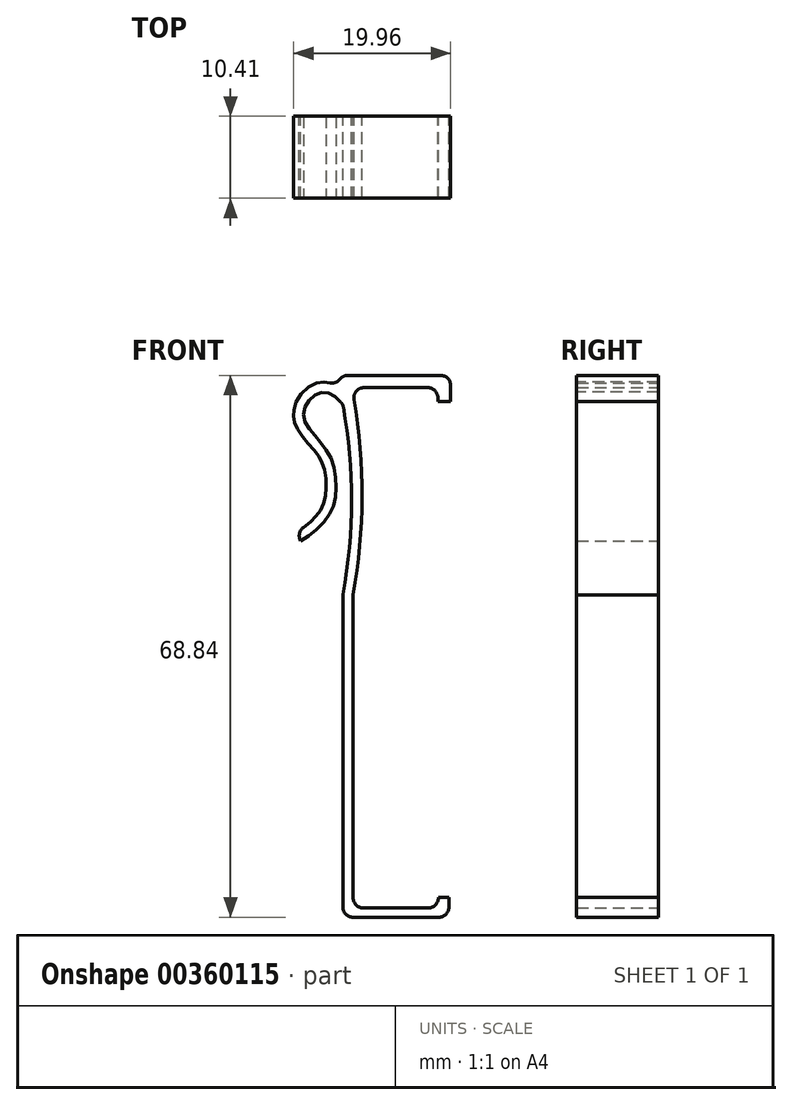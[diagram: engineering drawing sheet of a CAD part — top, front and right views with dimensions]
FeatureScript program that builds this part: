
annotation { "Feature Type Name" : "Feature", "Feature Type Description" : "" }
export const myFeature = defineFeature(function(context is Context, id is Id, definition is map)
    precondition{}
    {
        {
            var Q0;
            Q0=qCreatedBy(makeId("Front.planeOp"),FACE);
            var sketch = newSketch(context, id + "F0", { "sketchPlane" : qUnion([Q0])});
            skLineSegment(sketch, "E0", {"start": v(5, -38.43) * mm, "end": v(5, -40.97) * mm});
            skLineSegment(sketch, "E1", {"start": v(5, -40.97) * mm, "end": v(-8.46, -40.97) * mm});
            skLineSegment(sketch, "E2", {"start": v(-8.46, -40.97) * mm, "end": v(-8.46, 0.05) * mm});
            skFitSpline(sketch, "E3", {"points": [v(-8.49, 24.22) * mm, v(-10.38, 25.67) * mm, v(-12.43, 25.03) * mm, v(-13.45, 22.73) * mm, v(-12.1, 20.3) * mm, v(-10, 17.35) * mm, v(-9.36, 13.05) * mm, v(-10.53, 9.66) * mm, v(-13.86, 6.85) * mm], "startDerivative": vector(-14.07, 14.82) * mm, "endDerivative": vector(-23.04, -10.91) * mm});
            skFitSpline(sketch, "E4.0", {"points": [v(-7.57, 25.1) * mm, v(-7.7, 25.24) * mm, v(-8.04, 25.6) * mm, v(-8.57, 26.1) * mm, v(-9.1, 26.48) * mm, v(-9.47, 26.69) * mm, v(-9.8, 26.83) * mm, v(-10.08, 26.91) * mm, v(-10.36, 26.97) * mm, v(-10.74, 27.01) * mm, v(-11.2, 27) * mm, v(-11.9, 26.85) * mm, v(-12.69, 26.48) * mm, v(-13.49, 25.83) * mm, v(-14.12, 25.02) * mm, v(-14.5, 24.24) * mm, v(-14.68, 23.56) * mm, v(-14.73, 23.1) * mm, v(-14.73, 22.73) * mm, v(-14.7, 22.36) * mm, v(-14.6, 21.92) * mm, v(-14.42, 21.43) * mm, v(-14.12, 20.84) * mm, v(-13.68, 20.2) * mm, v(-13.11, 19.51) * mm, v(-12.57, 18.89) * mm, v(-12.06, 18.29) * mm, v(-11.61, 17.7) * mm, v(-11.31, 17.18) * mm, v(-11.12, 16.76) * mm, v(-10.95, 16.3) * mm, v(-10.77, 15.66) * mm, v(-10.64, 14.83) * mm, v(-10.6, 13.99) * mm, v(-10.6, 13.16) * mm, v(-10.7, 12.43) * mm, v(-10.85, 11.77) * mm, v(-11.08, 11.17) * mm, v(-11.35, 10.69) * mm, v(-11.63, 10.29) * mm, v(-11.97, 9.88) * mm, v(-12.46, 9.36) * mm, v(-13.12, 8.8) * mm, v(-13.8, 8.32) * mm, v(-14.22, 8.09) * mm, v(-14.4, 8) * mm]});
            skLineSegment(sketch, "E5", {"start": v(5.23, 24.52) * mm, "end": v(5.23, 27.6) * mm});
            skLineSegment(sketch, "E6.1", {"start": v(3.67, -38.43) * mm, "end": v(3.67, -39.78) * mm});
            skLineSegment(sketch, "E6.2", {"start": v(3.67, -39.78) * mm, "end": v(-7.17, -39.78) * mm});
            skLineSegment(sketch, "E6.3", {"start": v(-7.17, -39.78) * mm, "end": v(-7.17, 0) * mm});
            skLineSegment(sketch, "E7.0", {"start": v(3.6, 26.3) * mm, "end": v(-7.32, 26.3) * mm});
            skLineSegment(sketch, "E7.1", {"start": v(3.6, 24.52) * mm, "end": v(3.6, 26.3) * mm});
            skLineSegment(sketch, "E8", {"start": v(3.6, 24.52) * mm, "end": v(5.23, 24.52) * mm});
            skLineSegment(sketch, "E9", {"start": v(3.67, -38.43) * mm, "end": v(5, -38.43) * mm});
            skLineSegment(sketch, "E10", {"start": v(5.23, -76.05) * mm, "end": v(5, -38.43) * mm, "construction": true});
            skArc(sketch, "E11", {"start": v(-7.17, 0) * mm, "mid": v(-6.03, 13.16) * mm, "end": v(-7.32, 26.3) * mm});
            skArc(sketch, "E12", {"start": v(-8.46, 0.05) * mm, "mid": v(-7.36, 12.13) * mm, "end": v(-8.49, 24.22) * mm});
            skLineSegment(sketch, "E13", {"start": v(-14.33, 8.04) * mm, "end": v(-13.86, 6.85) * mm});
            skLineSegment(sketch, "E14", {"start": v(-8.6, 26.1) * mm, "end": v(-8.6, 27.87) * mm});
            skLineSegment(sketch, "E15", {"start": v(-8.6, 27.87) * mm, "end": v(5.23, 27.87) * mm});
            skLineSegment(sketch, "E16", {"start": v(5.23, 27.87) * mm, "end": v(5.23, 27.6) * mm});
            skSolve(sketch);
        }
        {
            var Q0;
            Q0 = qSketchRegion(id + "F0", true);
            extrude(context, id + "F1", {"entities" : qUnion([Q0]), "depth" : 10.4 * mm});
        }
        {
            var Q0;
            Q0=makeQuery(id+"F1.opExtrude","SWEPT_EDGE",EDGE,{"disambiguationData":[OSD([sQuery(id+"F0.wireOp",EDGE,"E6.2"),sQuery(id+"F0.wireOp",EDGE,"E6.3")])]});
            fillet(context, id + "F2", {"entities" : qUnion([Q0]), "radius" : 1.27 * mm, "tangentPropagation" : true, "allowEdgeOverflow" : false});
        }
        {
            var Q0;
            Q0=makeQuery(id+"F1.opExtrude","SWEPT_EDGE",EDGE,{"disambiguationData":[OSD([sQuery(id+"F0.wireOp",EDGE,"E6.1"),sQuery(id+"F0.wireOp",EDGE,"E6.2")])]});
            var Q1;
            Q1=makeQuery(id+"F1.opExtrude","SWEPT_EDGE",EDGE,{"disambiguationData":[OSD([sQuery(id+"F0.wireOp",EDGE,"E0"),sQuery(id+"F0.wireOp",EDGE,"E1")])]});
            var Q2;
            Q2=makeQuery(id+"F1.opExtrude","SWEPT_EDGE",EDGE,{"disambiguationData":[OSD([sQuery(id+"F0.wireOp",EDGE,"E1"),sQuery(id+"F0.wireOp",EDGE,"E2")])]});
            var Q3;
            Q3=makeQuery(id+"F1.opExtrude","SWEPT_EDGE",EDGE,{"disambiguationData":[OSD([sQuery(id+"F0.wireOp",EDGE,"E6.0"),sQuery(id+"F0.wireOp",EDGE,"E7.0")])]});
            var Q4;
            Q4=makeQuery(id+"F1.opExtrude","SWEPT_EDGE",EDGE,{"disambiguationData":[OSD([sQuery(id+"F0.wireOp",EDGE,"E4.0"),sQuery(id+"F0.wireOp",EDGE,"Rf88XzU9-4oze-62iC-AVGe-uAvs13QECtjz")])]});
            fillet(context, id + "F3", {"entities" : qUnion([Q0, Q1, Q2, Q3, Q4]), "radius" : 1.27 * mm, "tangentPropagation" : true, "allowEdgeOverflow" : false});
        }
        {
            var Q0;
            Q0=makeQuery(id+"F1.opExtrude","SWEPT_EDGE",EDGE,{"disambiguationData":[OSD([sQuery(id+"F0.wireOp",EDGE,"E3"),sQuery(id+"F0.wireOp",EDGE,"E12")])]});
            fillet(context, id + "F4", {"entities" : qUnion([Q0]), "radius" : 1.27 * mm, "tangentPropagation" : true, "allowEdgeOverflow" : false});
        }
        {
            var Q0;
            Q0=makeQuery(id+"F3.opFillet","BLEND_EDGE",EDGE,{"blendedFrom":[makeQuery(id+"F1.opExtrude","SWEPT_EDGE",EDGE,{"disambiguationData":[OSD([sQuery(id+"F0.wireOp",EDGE,"E4.0"),sQuery(id+"F0.wireOp",EDGE,"E14")])]}),makeQuery(id+"F1.opExtrude","SWEPT_FACE",FACE,{"disambiguationData":[OSD([sQuery(id+"F0.wireOp",EDGE,"E15")])]})],"blendedInto":[makeQuery(id+"F1.opExtrude","SWEPT_FACE",FACE,{"disambiguationData":[OSD([sQuery(id+"F0.wireOp",EDGE,"E15")])]})]});
            fillet(context, id + "F5", {"entities" : qUnion([Q0]), "radius" : 1.27 * mm, "tangentPropagation" : true, "allowEdgeOverflow" : false});
        }
        {
            var Q0;
            Q0=makeQuery(id+"F1.opExtrude","SWEPT_EDGE",EDGE,{"disambiguationData":[OSD([sQuery(id+"F0.wireOp",EDGE,"E15"),sQuery(id+"F0.wireOp",EDGE,"E16")])]});
            fillet(context, id + "F6", {"entities" : qUnion([Q0]), "radius" : 1.27 * mm, "tangentPropagation" : true, "allowEdgeOverflow" : false});
        }
    });
